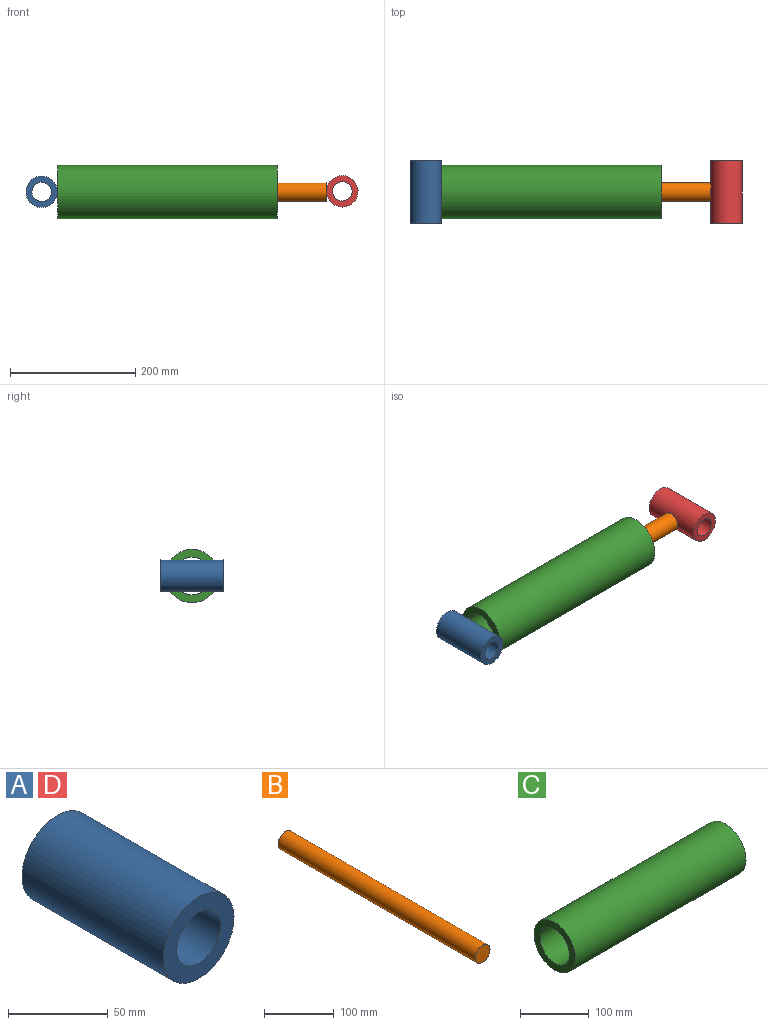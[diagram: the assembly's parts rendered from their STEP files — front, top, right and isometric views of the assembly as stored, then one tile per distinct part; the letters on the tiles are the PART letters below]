
ASSEMBLY  parts=4 mates=1
PART A: 4 faces, bbox 50x100x50 mm
  f0: cylinder r=15.5mm len=100mm, axis (0,1,0), area 9738.9mm2, adj f2,f3
  f1: cylinder r=25mm len=100mm, axis (0,1,0), area 15708mm2, adj f2,f3
  f2: plane 50x50mm, normal (0,-1,0), area 1208.7mm2, adj f0,f1
  f3: plane 50x50mm, normal (0,1,0), area 1208.7mm2, adj f0,f1
PART B: 3 faces, bbox 30x400x30 mm
  f0: cylinder r=15mm len=400mm, axis (0,1,0), area 37699.1mm2, adj f1,f2
  f1: plane 30x30mm, normal (0,-1,0), area 706.9mm2, adj f0
  f2: plane 30x30mm, normal (0,1,0), area 706.9mm2, adj f0
PART C: 4 faces, bbox 350x85x85 mm
  f0: plane 85x85mm, normal (-1,0,0), area 2847.1mm2, adj f1,f3
  f1: cylinder r=42.5mm len=350mm, axis (-1,0,0), area 93462.4mm2, adj f0,f2
  f2: plane 85x85mm, normal (1,0,0), area 2847.1mm2, adj f1,f3
  f3: cylinder r=30mm len=350mm, axis (-1,0,0), area 65973.4mm2, adj f0,f2
PART D: same geometry as A
PLACE A t=(-364.29,50,103.78)mm
PLACE B rot(axis=(0,0,1),90deg) t=(-309.78,0,103.51)mm
PLACE C t=(-229.36,0,53.51)mm
PLACE D t=(115.4,50,104.58)mm
MATE slider B.f0 <-> C.f1  axis (-1,0,0) through (-109.78,0,103.51)mm
